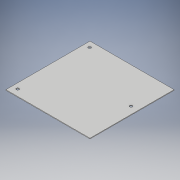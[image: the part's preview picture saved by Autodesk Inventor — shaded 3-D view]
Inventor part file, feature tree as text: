
AUTODESK INVENTOR PART (.ipt)
format: ipt  version: 2018 (Build 220112000, 112)  size: 102,912 bytes
history: native  units: in
note: dims shown in document units (in); Inventor stores cm internally (conversion verified against a paired STEP export)
features: extrude x2, sketch x2
ambient origin geometry x8: Origin, YZ Plane, XZ Plane, XY Plane, X Axis, Y Axis, Z Axis, Center Point
bodies: Body1 (feature_tree)
feature tree (4):
  extrude  "Extrusion2"  Depth=3.937in
  extrude  "Extrusion3"  Depth=0.031in
  sketch  "Sketch2"  dims[d4=3.937in d5=3.937in]
  sketch  "Sketch3"  dims[d6=0.031in d7=0.0in d8=0.1285in d9=0.1285in d10=0.1285in d11=0.0in d12=0.0in]
